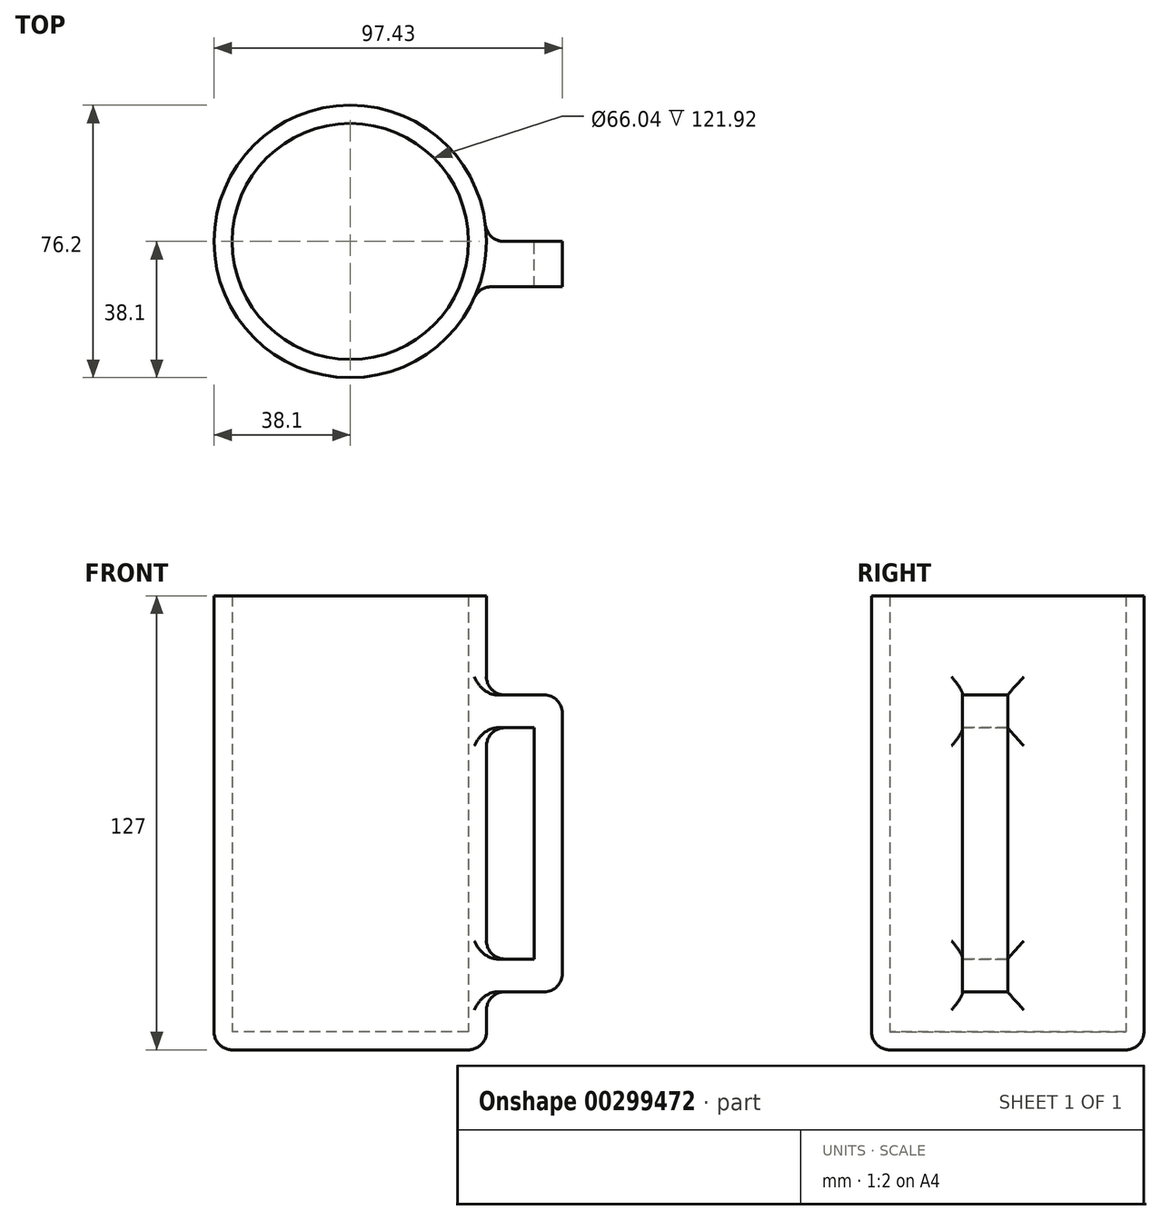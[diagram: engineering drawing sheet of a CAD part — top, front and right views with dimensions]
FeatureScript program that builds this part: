
annotation { "Feature Type Name" : "Feature", "Feature Type Description" : "" }
export const myFeature = defineFeature(function(context is Context, id is Id, definition is map)
    precondition{}
    {
        {
            var Q0;
            Q0=qCreatedBy(makeId("Top.planeOp"),FACE);
            var sketch = newSketch(context, id + "F0", { "sketchPlane" : qUnion([Q0])});
            skCircle(sketch, "E0", {"center": v(0, 0) * mm, "radius": 38.1 * mm});
            skSolve(sketch);
        }
        {
            var Q0;
            Q0=makeQuery(id+"F0.imprint","IMPRINT",FACE,{"disambiguationData":[TD([[makeQuery(id+"F0.imprint","IMPRINT",EDGE,{"derivedFrom":sQuery(id+"F0.wireOp",EDGE,"E0")}),1.0]])]});
            extrude(context, id + "F1", {"entities" : qUnion([Q0]), "depth" : 127 * mm});
        }
        {
            var Q0;
            Q0=makeQuery(id+"F1.opExtrude","CAP_FACE",FACE,{"disambiguationData":[OSD([sQuery(id+"F0.wireOp",EDGE,"E0")])],"isStart":false});
            shell(context, id + "F2", {"entities" : qUnion([Q0]), "thickness" : 5.08 * mm});
        }
        {
            var Q0;
            Q0=qCreatedBy(makeId("Front.planeOp"),FACE);
            var sketch = newSketch(context, id + "F3", { "sketchPlane" : qUnion([Q0])});
            skLineSegment(sketch, "E1", {"start": v(35.64, 99.24) * mm, "end": v(59.33, 99.24) * mm});
            skLineSegment(sketch, "E2", {"start": v(59.33, 99.24) * mm, "end": v(59.33, 16.23) * mm});
            skLineSegment(sketch, "E3", {"start": v(59.33, 16.23) * mm, "end": v(35.64, 16.23) * mm});
            skLineSegment(sketch, "E4", {"start": v(35.64, 16.23) * mm, "end": v(35.64, 25.4) * mm});
            skLineSegment(sketch, "E5", {"start": v(51.42, 25.4) * mm, "end": v(35.64, 25.4) * mm});
            skLineSegment(sketch, "E6", {"start": v(51.42, 25.4) * mm, "end": v(51.42, 90.07) * mm});
            skLineSegment(sketch, "E7", {"start": v(51.42, 90.07) * mm, "end": v(35.64, 90.07) * mm});
            skLineSegment(sketch, "E8", {"start": v(35.64, 90.07) * mm, "end": v(35.64, 99.24) * mm});
            skSolve(sketch);
        }
        {
            var Q0;
            Q0 = qSketchRegion(id + "F3", true);
            extrude(context, id + "F4", {"entities" : qUnion([Q0]), "operationType" : NewBodyOperationType.ADD, "depth" : 12.7 * mm});
        }
        {
            var Q0;
            Q0=makeQuery(id+"F4.boolean.opBoolean","INTERSECT",EDGE,{"disambiguationData":[OD(0.0)],"derivedFrom":[makeQuery(id+"F1.opExtrude","SWEPT_FACE",FACE,{"disambiguationData":[OSD([sQuery(id+"F0.wireOp",EDGE,"E0")])]}),makeQuery(id+"F4.opExtrude","CAP_FACE",FACE,{"disambiguationData":[OSD([sQuery(id+"F3.wireOp",EDGE,"E1"),sQuery(id+"F3.wireOp",EDGE,"E2"),sQuery(id+"F3.wireOp",EDGE,"E3"),sQuery(id+"F3.wireOp",EDGE,"E4"),sQuery(id+"F3.wireOp",EDGE,"E5"),sQuery(id+"F3.wireOp",EDGE,"E6"),sQuery(id+"F3.wireOp",EDGE,"E7"),sQuery(id+"F3.wireOp",EDGE,"E8")])],"isStart":false})]});
            var Q1;
            Q1=makeQuery(id+"F4.boolean.opBoolean","INTERSECT",EDGE,{"derivedFrom":[makeQuery(id+"F1.opExtrude","SWEPT_FACE",FACE,{"disambiguationData":[OSD([sQuery(id+"F0.wireOp",EDGE,"E0")])]}),makeQuery(id+"F4.opExtrude","SWEPT_FACE",FACE,{"disambiguationData":[OSD([sQuery(id+"F3.wireOp",EDGE,"E1")])]})]});
            var Q2;
            Q2=makeQuery(id+"F4.boolean.opBoolean","INTERSECT",EDGE,{"derivedFrom":[makeQuery(id+"F1.opExtrude","SWEPT_FACE",FACE,{"disambiguationData":[OSD([sQuery(id+"F0.wireOp",EDGE,"E0")])]}),makeQuery(id+"F4.opExtrude","SWEPT_FACE",FACE,{"disambiguationData":[OSD([sQuery(id+"F3.wireOp",EDGE,"E7")])]})]});
            var Q3;
            Q3=makeQuery(id+"F4.boolean.opBoolean","INTERSECT",EDGE,{"derivedFrom":[makeQuery(id+"F1.opExtrude","SWEPT_FACE",FACE,{"disambiguationData":[OSD([sQuery(id+"F0.wireOp",EDGE,"E0")])]}),makeQuery(id+"F4.opExtrude","SWEPT_FACE",FACE,{"disambiguationData":[OSD([sQuery(id+"F3.wireOp",EDGE,"E3")])]})]});
            var Q4;
            Q4=makeQuery(id+"F4.boolean.opBoolean","INTERSECT",EDGE,{"disambiguationData":[OD(1.0)],"derivedFrom":[makeQuery(id+"F1.opExtrude","SWEPT_FACE",FACE,{"disambiguationData":[OSD([sQuery(id+"F0.wireOp",EDGE,"E0")])]}),makeQuery(id+"F4.opExtrude","CAP_FACE",FACE,{"disambiguationData":[OSD([sQuery(id+"F3.wireOp",EDGE,"E1"),sQuery(id+"F3.wireOp",EDGE,"E2"),sQuery(id+"F3.wireOp",EDGE,"E3"),sQuery(id+"F3.wireOp",EDGE,"E4"),sQuery(id+"F3.wireOp",EDGE,"E5"),sQuery(id+"F3.wireOp",EDGE,"E6"),sQuery(id+"F3.wireOp",EDGE,"E7"),sQuery(id+"F3.wireOp",EDGE,"E8")])],"isStart":false})]});
            var Q5;
            Q5=makeQuery(id+"F4.boolean.opBoolean","INTERSECT",EDGE,{"derivedFrom":[makeQuery(id+"F1.opExtrude","SWEPT_FACE",FACE,{"disambiguationData":[OSD([sQuery(id+"F0.wireOp",EDGE,"E0")])]}),makeQuery(id+"F4.opExtrude","SWEPT_FACE",FACE,{"disambiguationData":[OSD([sQuery(id+"F3.wireOp",EDGE,"E5")])]})]});
            var Q6;
            Q6=makeQuery(id+"F4.boolean.opBoolean","INTERSECT",EDGE,{"disambiguationData":[OD(1.0)],"derivedFrom":[makeQuery(id+"F1.opExtrude","SWEPT_FACE",FACE,{"disambiguationData":[OSD([sQuery(id+"F0.wireOp",EDGE,"E0")])]}),makeQuery(id+"F4.opExtrude","CAP_FACE",FACE,{"disambiguationData":[OSD([sQuery(id+"F3.wireOp",EDGE,"E1"),sQuery(id+"F3.wireOp",EDGE,"E2"),sQuery(id+"F3.wireOp",EDGE,"E3"),sQuery(id+"F3.wireOp",EDGE,"E4"),sQuery(id+"F3.wireOp",EDGE,"E5"),sQuery(id+"F3.wireOp",EDGE,"E6"),sQuery(id+"F3.wireOp",EDGE,"E7"),sQuery(id+"F3.wireOp",EDGE,"E8")])],"isStart":true})]});
            var Q7;
            Q7=makeQuery(id+"F4.boolean.opBoolean","INTERSECT",EDGE,{"disambiguationData":[OD(0.0)],"derivedFrom":[makeQuery(id+"F1.opExtrude","SWEPT_FACE",FACE,{"disambiguationData":[OSD([sQuery(id+"F0.wireOp",EDGE,"E0")])]}),makeQuery(id+"F4.opExtrude","CAP_FACE",FACE,{"disambiguationData":[OSD([sQuery(id+"F3.wireOp",EDGE,"E1"),sQuery(id+"F3.wireOp",EDGE,"E2"),sQuery(id+"F3.wireOp",EDGE,"E3"),sQuery(id+"F3.wireOp",EDGE,"E4"),sQuery(id+"F3.wireOp",EDGE,"E5"),sQuery(id+"F3.wireOp",EDGE,"E6"),sQuery(id+"F3.wireOp",EDGE,"E7"),sQuery(id+"F3.wireOp",EDGE,"E8")])],"isStart":true})]});
            var Q8;
            Q8=makeQuery(id+"F4.opExtrude","SWEPT_EDGE",EDGE,{"disambiguationData":[OSD([sQuery(id+"F3.wireOp",EDGE,"E1"),sQuery(id+"F3.wireOp",EDGE,"E2")])]});
            var Q9;
            Q9=makeQuery(id+"F4.opExtrude","SWEPT_EDGE",EDGE,{"disambiguationData":[OSD([sQuery(id+"F3.wireOp",EDGE,"E2"),sQuery(id+"F3.wireOp",EDGE,"E3")])]});
            var Q10;
            Q10=makeQuery(id+"F1.opExtrude","CAP_EDGE",EDGE,{"disambiguationData":[OSD([sQuery(id+"F0.wireOp",EDGE,"E0")])],"isStart":true});
            fillet(context, id + "F5", {"entities" : qUnion([Q0, Q1, Q2, Q3, Q4, Q5, Q6, Q7, Q8, Q9, Q10]), "radius" : 5.08 * mm, "tangentPropagation" : true, "allowEdgeOverflow" : false});
        }
    });
